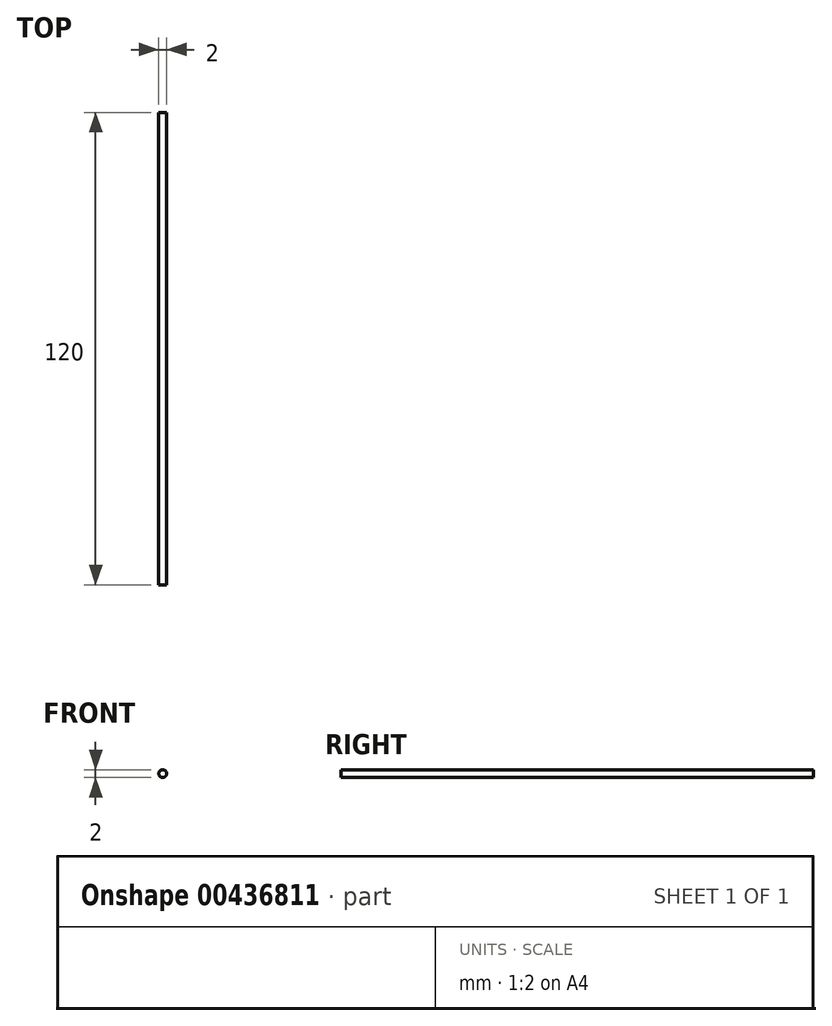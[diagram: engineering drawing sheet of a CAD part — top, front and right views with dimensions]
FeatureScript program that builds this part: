
annotation { "Feature Type Name" : "Feature", "Feature Type Description" : "" }
export const myFeature = defineFeature(function(context is Context, id is Id, definition is map)
    precondition{}
    {
        {
            var Q0;
            Q0=qCreatedBy(makeId("Front.planeOp"),FACE);
            var sketch = newSketch(context, id + "F0", { "sketchPlane" : qUnion([Q0])});
            skCircle(sketch, "E0", {"center": v(0, 0) * mm, "radius": 1 * mm});
            skSolve(sketch);
        }
        {
            var Q0;
            Q0 = qSketchRegion(id + "F0", true);
            extrude(context, id + "F1", {"entities" : qUnion([Q0]), "depth" : 120 * mm});
        }
    });
